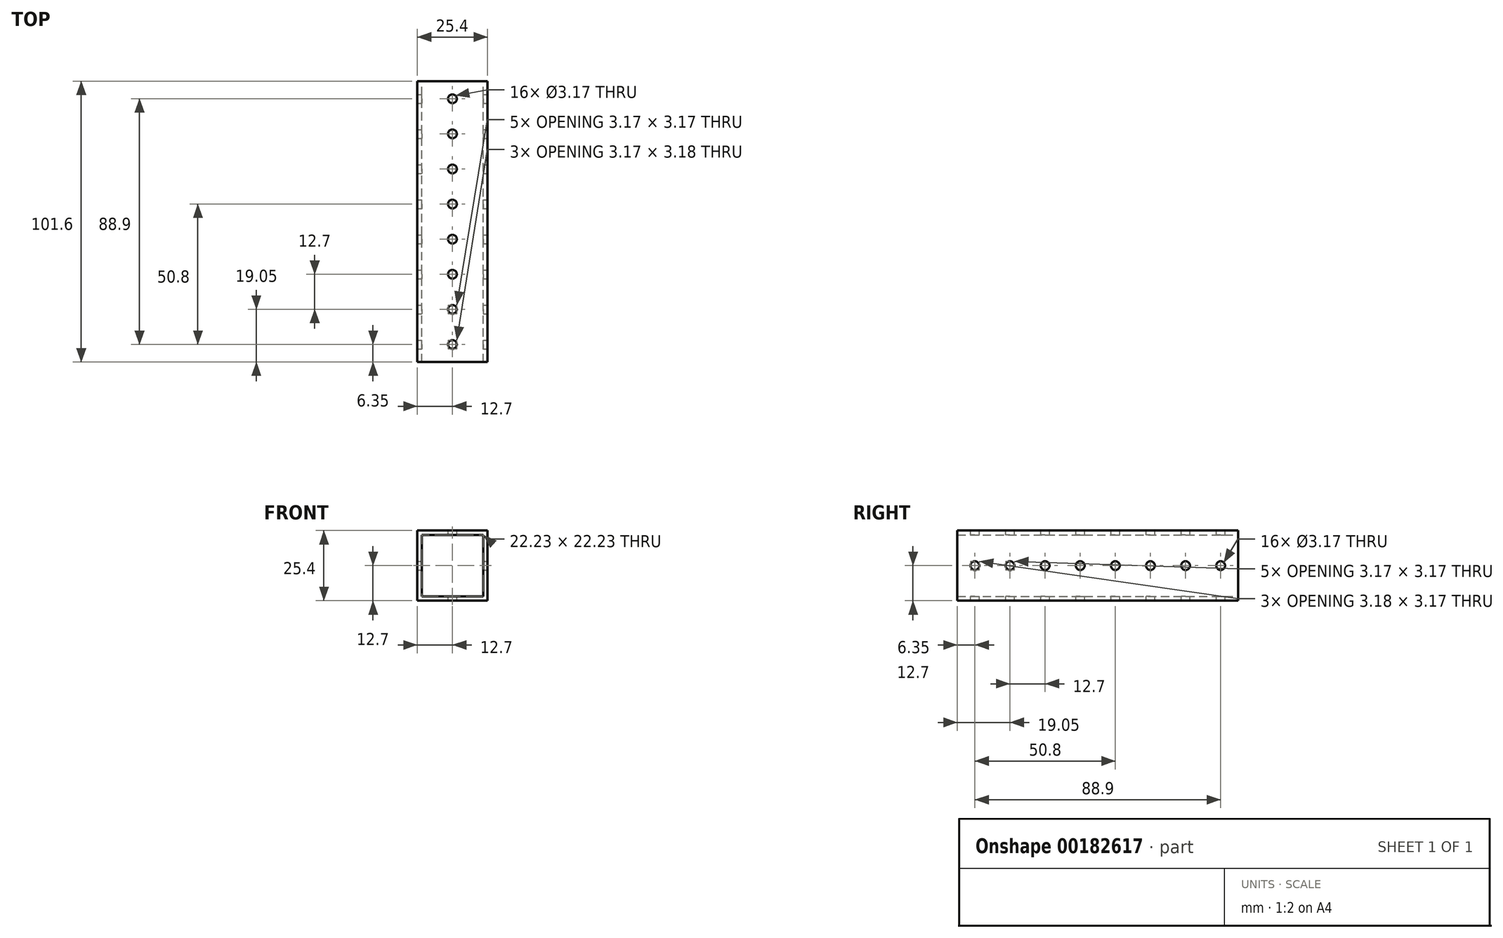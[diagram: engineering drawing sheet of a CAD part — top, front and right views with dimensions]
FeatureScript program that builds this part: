
annotation { "Feature Type Name" : "Feature", "Feature Type Description" : "" }
export const myFeature = defineFeature(function(context is Context, id is Id, definition is map)
    precondition{}
    {
        {
            var Q0;
            Q0=qCreatedBy(makeId("Front.planeOp"),FACE);
            var sketch = newSketch(context, id + "F0", { "sketchPlane" : qUnion([Q0])});
            skLineSegment(sketch, "E0.bottom", {"start": v(12.7, -12.7) * mm, "end": v(-12.7, -12.7) * mm});
            skLineSegment(sketch, "E0.top", {"start": v(12.7, 12.7) * mm, "end": v(-12.7, 12.7) * mm});
            skLineSegment(sketch, "E0.left", {"start": v(12.7, -12.7) * mm, "end": v(12.7, 12.7) * mm});
            skLineSegment(sketch, "E0.right", {"start": v(-12.7, -12.7) * mm, "end": v(-12.7, 12.7) * mm});
            skPoint(sketch, "E0.middle", {"position": v(0, 0) * mm});
            skLineSegment(sketch, "E1.bottom", {"start": v(11.11, -11.11) * mm, "end": v(-11.11, -11.11) * mm});
            skLineSegment(sketch, "E1.top", {"start": v(11.11, 11.11) * mm, "end": v(-11.11, 11.11) * mm});
            skLineSegment(sketch, "E1.left", {"start": v(11.11, -11.11) * mm, "end": v(11.11, 11.11) * mm});
            skLineSegment(sketch, "E1.right", {"start": v(-11.11, -11.11) * mm, "end": v(-11.11, 11.11) * mm});
            skSolve(sketch);
        }
        {
            var Q0;
            Q0 = qSketchRegion(id + "F0", true);
            extrude(context, id + "F1", {"entities" : qUnion([Q0]), "depth" : 101.6 * mm});
        }
        {
            var Q0;
            Q0=makeQuery(id+"F1.opExtrude","SWEPT_FACE",FACE,{"disambiguationData":[OSD([sQuery(id+"F0.wireOp",EDGE,"E0.top")])]});
            var sketch = newSketch(context, id + "F2", { "sketchPlane" : qUnion([Q0])});
            skCircle(sketch, "E2", {"center": v(0, -6.35) * mm, "radius": 1.59 * mm});
            skCircle(sketch, "E3", {"center": v(0, -19.05) * mm, "radius": 1.59 * mm});
            skCircle(sketch, "E4", {"center": v(0, -31.75) * mm, "radius": 1.59 * mm});
            skCircle(sketch, "E5", {"center": v(0, -44.45) * mm, "radius": 1.59 * mm});
            skCircle(sketch, "E6.MirrorC", {"center": v(0, -57.15) * mm, "radius": 1.59 * mm});
            skCircle(sketch, "E7.MirrorC", {"center": v(0, -69.85) * mm, "radius": 1.59 * mm});
            skCircle(sketch, "E8.MirrorC", {"center": v(0, -82.55) * mm, "radius": 1.59 * mm});
            skCircle(sketch, "E9.MirrorC", {"center": v(0, -95.25) * mm, "radius": 1.59 * mm});
            skSolve(sketch);
        }
        {
            var Q0;
            Q0 = qSketchRegion(id + "F2", true);
            extrude(context, id + "F3", {"entities" : qUnion([Q0]), "operationType" : NewBodyOperationType.REMOVE, "oppositeDirection" : true, "depth" : 25.4 * mm});
        }
        {
            var Q0;
            Q0=makeQuery(id+"F1.opExtrude","SWEPT_FACE",FACE,{"disambiguationData":[OSD([sQuery(id+"F0.wireOp",EDGE,"E0.left")])]});
            var sketch = newSketch(context, id + "F4", { "sketchPlane" : qUnion([Q0])});
            skCircle(sketch, "E10", {"center": v(-6.35, 0) * mm, "radius": 1.59 * mm});
            skCircle(sketch, "E11", {"center": v(-19.05, 0) * mm, "radius": 1.59 * mm});
            skCircle(sketch, "E12", {"center": v(-31.75, 0) * mm, "radius": 1.59 * mm});
            skCircle(sketch, "E13", {"center": v(-44.45, 0) * mm, "radius": 1.59 * mm});
            skCircle(sketch, "E14.MirrorC", {"center": v(-57.15, 0) * mm, "radius": 1.59 * mm});
            skCircle(sketch, "E15.MirrorC", {"center": v(-69.85, 0) * mm, "radius": 1.59 * mm});
            skCircle(sketch, "E16.MirrorC", {"center": v(-82.55, 0) * mm, "radius": 1.59 * mm});
            skCircle(sketch, "E17.MirrorC", {"center": v(-95.25, 0) * mm, "radius": 1.59 * mm});
            skSolve(sketch);
        }
        {
            var Q0;
            Q0 = qSketchRegion(id + "F4", true);
            extrude(context, id + "F5", {"entities" : qUnion([Q0]), "operationType" : NewBodyOperationType.REMOVE, "oppositeDirection" : true, "depth" : 25.4 * mm});
        }
    });
